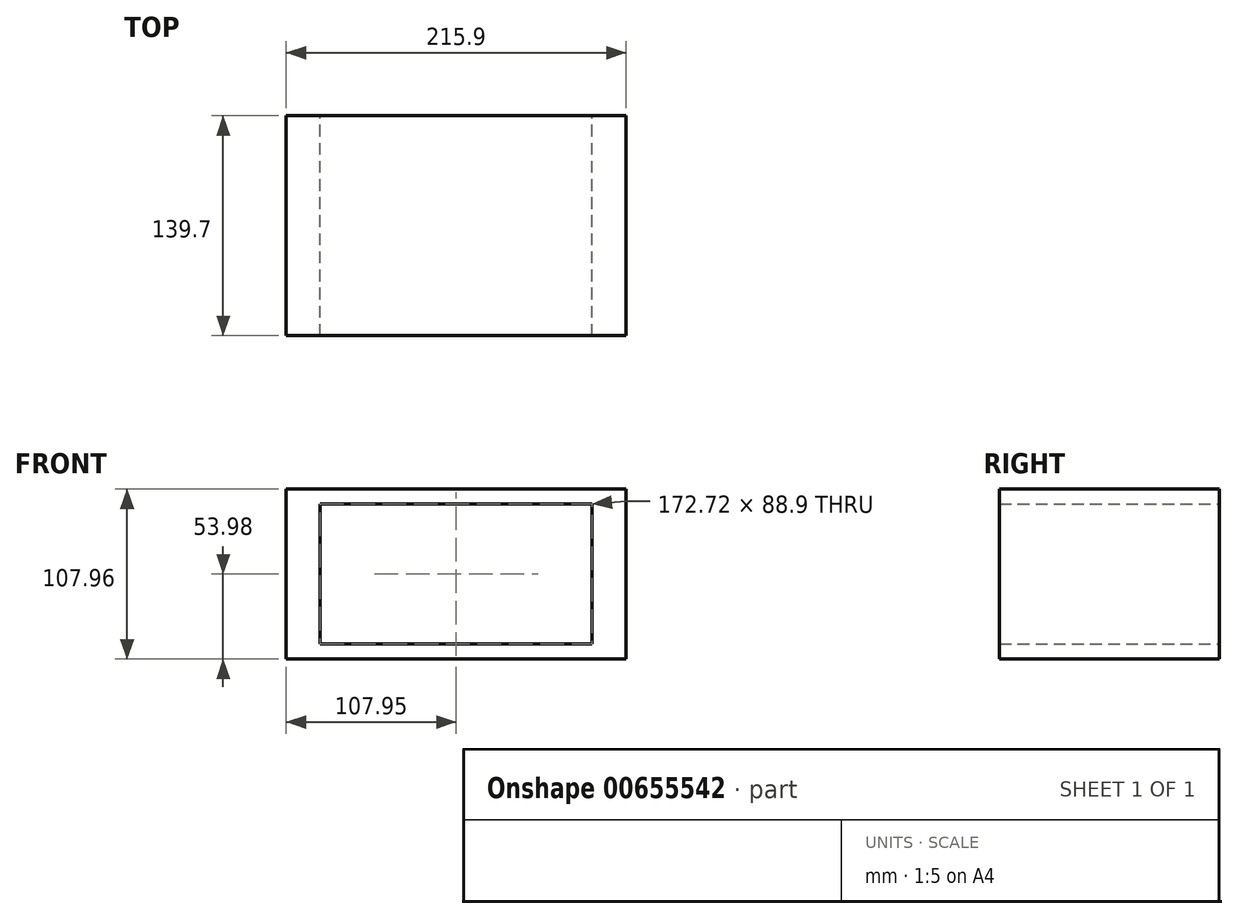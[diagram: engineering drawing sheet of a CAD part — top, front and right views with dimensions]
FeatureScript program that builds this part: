
annotation { "Feature Type Name" : "Feature", "Feature Type Description" : "" }
export const myFeature = defineFeature(function(context is Context, id is Id, definition is map)
    precondition{}
    {
        {
            var Q0;
            Q0=qCreatedBy(makeId("Front.planeOp"),FACE);
            var sketch = newSketch(context, id + "F0", { "sketchPlane" : qUnion([Q0])});
            skLineSegment(sketch, "E0.bottom", {"start": v(86.36, -44.45) * mm, "end": v(-86.36, -44.45) * mm});
            skLineSegment(sketch, "E0.top", {"start": v(86.36, 44.45) * mm, "end": v(-86.36, 44.45) * mm});
            skLineSegment(sketch, "E0.left", {"start": v(86.36, -44.45) * mm, "end": v(86.36, 44.45) * mm});
            skLineSegment(sketch, "E0.right", {"start": v(-86.36, -44.45) * mm, "end": v(-86.36, 44.45) * mm});
            skPoint(sketch, "E0.middle", {"position": v(0, 0) * mm});
            skLineSegment(sketch, "E1.bottom", {"start": v(107.95, -53.97) * mm, "end": v(-107.95, -53.98) * mm});
            skLineSegment(sketch, "E1.top", {"start": v(107.95, 53.98) * mm, "end": v(-107.95, 53.97) * mm});
            skLineSegment(sketch, "E1.left", {"start": v(107.95, -53.97) * mm, "end": v(107.95, 53.98) * mm});
            skLineSegment(sketch, "E1.right", {"start": v(-107.95, -53.98) * mm, "end": v(-107.95, 53.97) * mm});
            skSolve(sketch);
        }
        {
            var Q0;
            Q0 = qSketchRegion(id + "F0", true);
            extrude(context, id + "F1", {"entities" : qUnion([Q0]), "depth" : 139.7 * mm, "offsetDistance" : 25.4 * mm});
        }
    });
